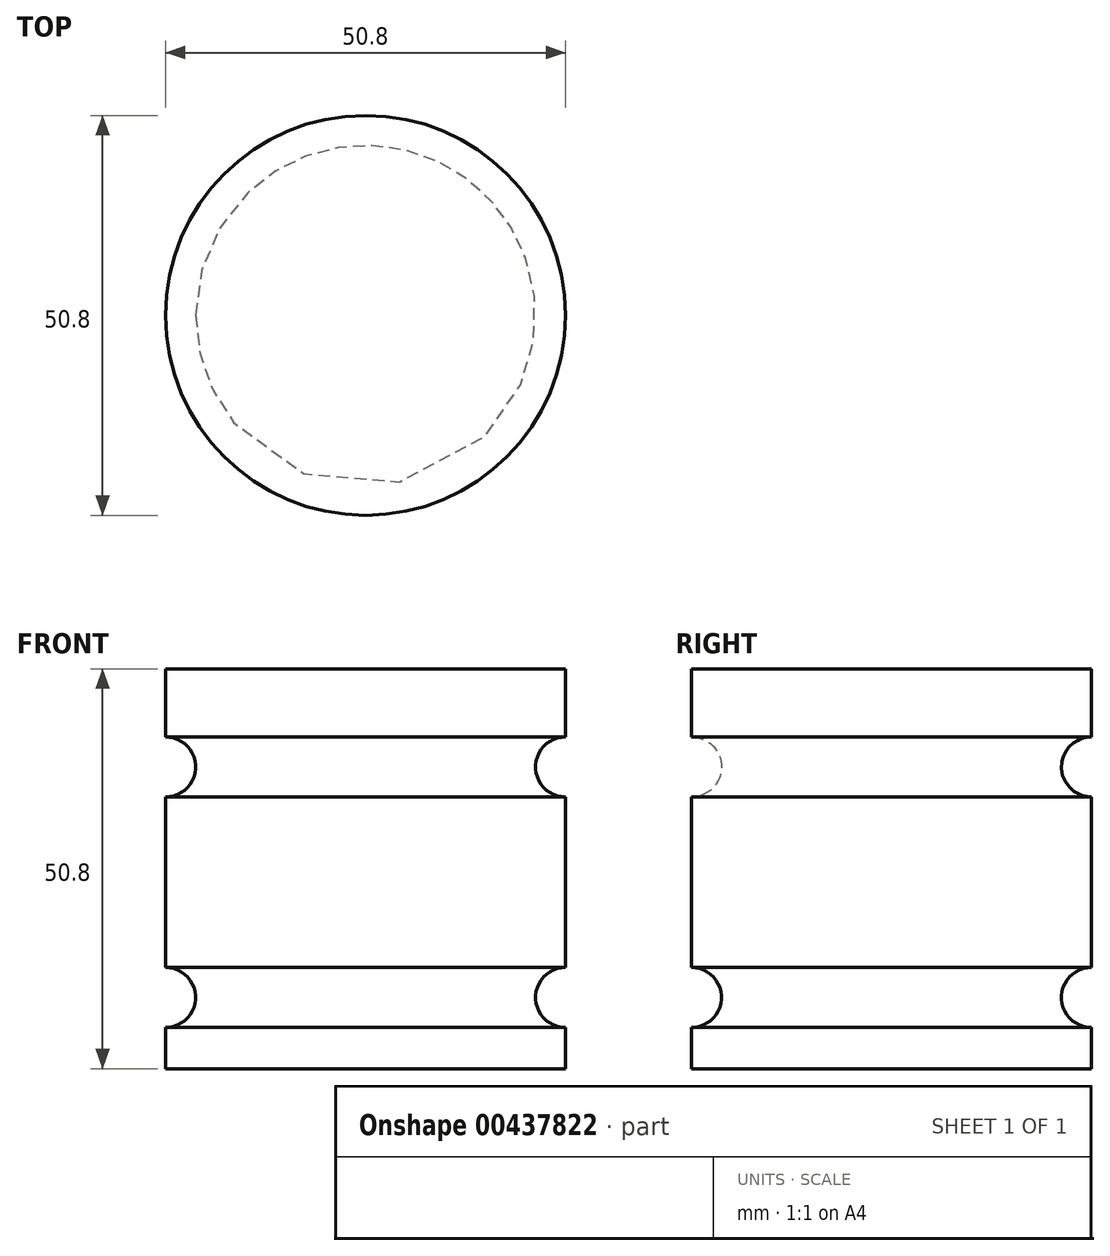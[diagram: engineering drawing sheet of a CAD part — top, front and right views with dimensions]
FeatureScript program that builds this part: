
annotation { "Feature Type Name" : "Feature", "Feature Type Description" : "" }
export const myFeature = defineFeature(function(context is Context, id is Id, definition is map)
    precondition{}
    {
        {
            var Q0;
            Q0=qCreatedBy(makeId("Front.planeOp"),FACE);
            var sketch = newSketch(context, id + "F0", { "sketchPlane" : qUnion([Q0])});
            skLineSegment(sketch, "E0.bottom", {"start": v(0, 0) * mm, "end": v(-25.4, 0) * mm});
            skLineSegment(sketch, "E0.top", {"start": v(0, 50.8) * mm, "end": v(-25.4, 50.8) * mm});
            skLineSegment(sketch, "E0.left", {"start": v(0, 0) * mm, "end": v(0, 5.24) * mm});
            skLineSegment(sketch, "E0.right", {"start": v(-25.4, 0) * mm, "end": v(-25.4, 50.8) * mm});
            skArc(sketch, "E1", {"start": v(0, 42.14) * mm, "mid": v(-3.81, 38.33) * mm, "end": v(0, 34.52) * mm});
            skArc(sketch, "E2", {"start": v(0, 12.86) * mm, "mid": v(-3.81, 9.05) * mm, "end": v(0, 5.24) * mm});
            skLineSegment(sketch, "E3.trimOffspring", {"start": v(0, 42.14) * mm, "end": v(0, 50.8) * mm});
            skLineSegment(sketch, "E4.trimOffspring", {"start": v(0, 12.86) * mm, "end": v(0, 34.52) * mm});
            skSolve(sketch);
        }
        {
            var Q0;
            Q0 = qSketchRegion(id + "F0", true);
            var Q1;
            Q1=sQuery(id+"F0.wireOp",EDGE,"E0.right");
            revolve(context, id + "F1", {"entities" : qUnion([Q0]), "axis" : qUnion([Q1]), "revolveType" : RevolveType.FULL});
        }
    });
